# Revit family: Pump_Commercial-Sewage_Dewatering-Zoeller-64HD_Single_Seal_4-Series
name_source: partatom
category: Mechanical Equipment
revit_build: Autodesk Revit 2014 (Build: 20130308_1515(x64)
units: mm (PartAtom-declared; Revit-internal decimal feet)

## types (7) — shared parameters
Assembly Code = D2090
Connection Description = 4" Horizontal Discharge
Default Elevation = 0"
Description = Heavy Duty Solids-Handling Pumps
Discharge Diameter = 4"
Discharge Radius = 2"
Flange = ANSI B16.1
Height = 46 1/8"
Hertz = 60
High Temperature (5-10 BHP) = No
Impeller Type = 2 Vane Enclosed
Installation Type = Floor Mounted
Insulation = Class F
Inverted Duty = No
Inverted Duty Submersible = No
Length = 25 5/8"
Manufacturer = Zoeller
Material = Cast Iron-Zoeller-Powder Coated Epoxy
Max. Stator Temp. = 311 °F
Max. Water Temp. = 104 °F
Min. Recommended Fluid Level = 36"
Moisture Detection = Moisture Sensing Probes
Motor Design Letter = NEMA B
Motor Shaft = 416 SS
Motor Thermal Shutoff = Thermal Sensors With Automatic Reset
Motor Type = Standard Submersible
O-Rings (Optional) Viton = No
O-Rings and Cover Gasket = Buna-N
Operation = Non-Automatic
Phase = 3
Power Cord = 25' (7.6 m) #2-4 SO
Price = Prices may vary. Please consult Manufacturer Representative for most up-to-date price list.
Pump Net Weight: lbs. (kg) = 825 lbs. (374 kg)
RPM = 1725
Sensor Cord Size = #16-5 SO
Shaft Seal (Standard) = Carbon/Ceramic
Shaft Seal Lower (Options) = Silicon Carbide
Shaft Seal Upper (Options) = Silicon Carbide
Solid Size = 4"- 3-1/8"
Tandem Seals = Standard
Trimmed Impeller = No
URL = http://www.zoellerpumps.com
Warranty Information = 36 Months (Limited)
Waste Connection = Yes
Width = 22 1/2"

## per-type parameters (varying)
| type | Amps | Apparent Load | Flow Rate | Impeller Diameter | Locked Rotor Amps (Voltage Dependant) | Max. Flow at Min. Head | Max. Head | Maximum KW Input | Model | Motor | NEC Locked Rotor Code | Service Factor | Voltage |
| F6424 - 230V/3Ph/68A/25BHP | 68 A | 15640 VA | 960 GPM | 9 7/8" | 314 | 960GPM @ 55' | 112' | 24.2 | F6424 | 25 BHP | F | 1.2 | 230 V |
| G6424 - 460V/3Ph/34A/25BHP | 34 A | 15640 VA | 960 GPM | 9 7/8" | 157 | 960GPM @ 55' | 112' | 24.2 | G6424 | 25 BHP | F | 1.2 | 460 V |
| F6425 - 230V/3Ph/80A/30BHP | 80 A | 18400 VA | 1130 GPM | 10 3/8" | 360 | 900GPM @ 75' | 120' | 28.1 | F6425 | 30 BHP | E | 1.2 | 230 V |
| G6425 - 460V/3Ph/40A/30BHP | 40 A | 18400 VA | 1130 GPM | 10 3/8" | 180 | 900GPM @ 75' | 120' | 28.1 | G6425 | 30 BHP | E | 1.2 | 460 V |
| G6426 - 460V/3Ph/52A/40BHP | 52 A | 23920 VA | 980 GPM | 11 3/8" | 240 | 980GPM @ 95' | 145' | 36 | G6426 | 40 BHP | E | 1.2 | 460 V |
| G6427 - 460V/3Ph/62A/50BHP | 62 A | 28520 VA | 1000 GPM | 12 1/8" | 278 | 1000GPM @ 110' | 165' | 42.5 | G6427 | 50 BHP | D | 1.2 | 460 V |
| G6428 - 460V/3Ph/75A/60BHP | 75 A | 34500 VA | 970 GPM | 12 7/8" | 278 | 970GPM @ 133' | 190' | 50 | G6428 | 60 BHP | C | 1.0 | 460 V |

## geometry (parser evidence)
native form markers: Sweep x1
no freeform markers — native parametric forms only
